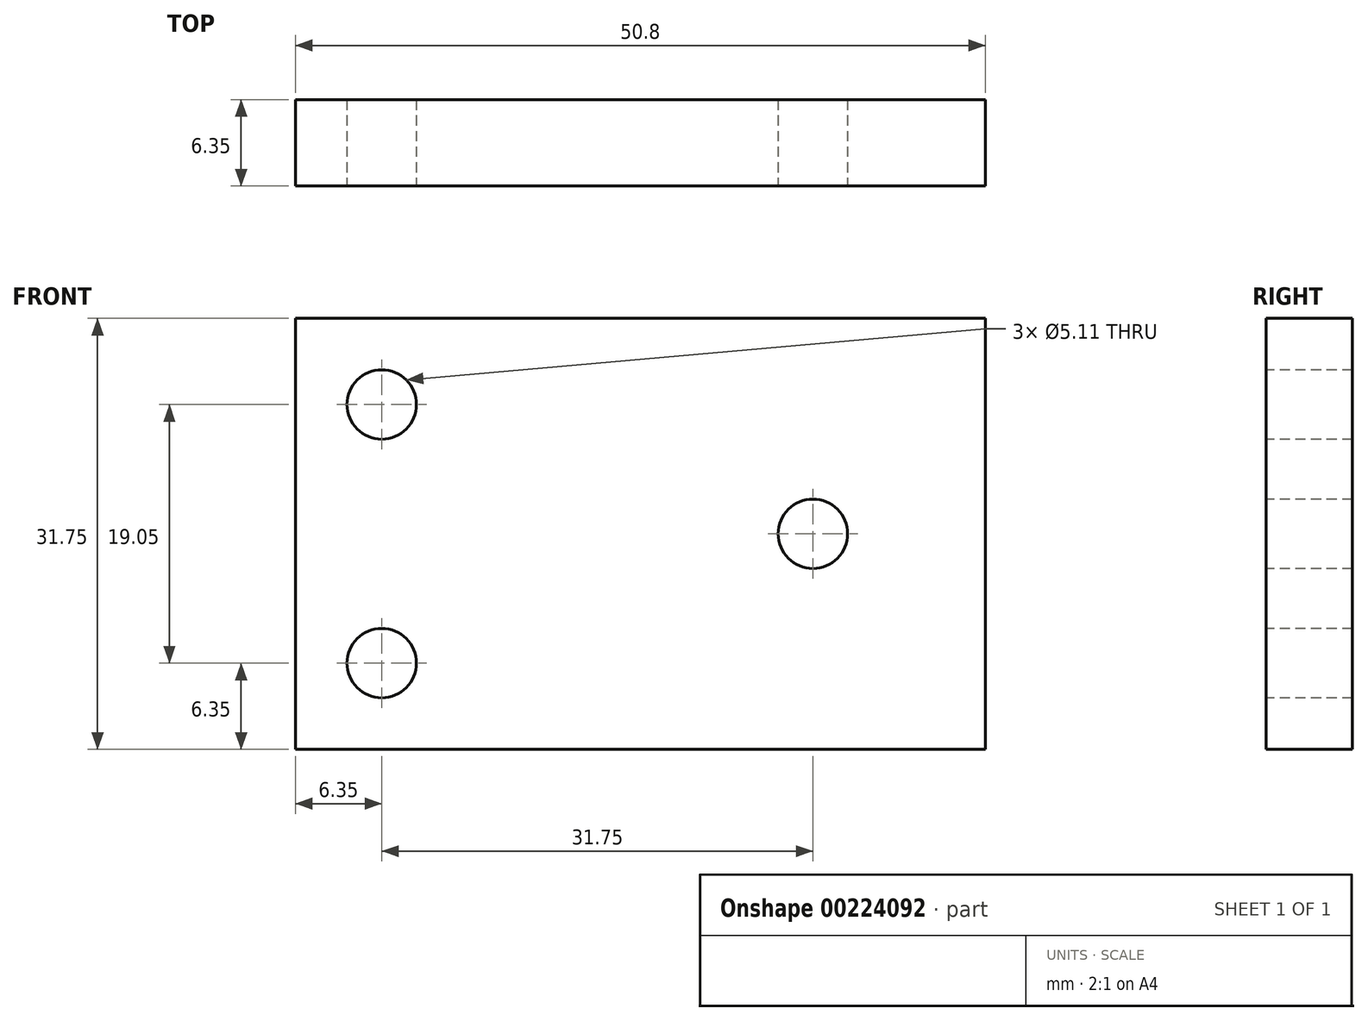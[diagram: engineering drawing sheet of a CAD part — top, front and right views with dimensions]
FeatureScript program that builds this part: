
annotation { "Feature Type Name" : "Feature", "Feature Type Description" : "" }
export const myFeature = defineFeature(function(context is Context, id is Id, definition is map)
    precondition{}
    {
        {
            var Q0;
            Q0=qCreatedBy(makeId("Front.planeOp"),FACE);
            var sketch = newSketch(context, id + "F0", { "sketchPlane" : qUnion([Q0])});
            skLineSegment(sketch, "E0.bottom", {"start": v(0, 0) * mm, "end": v(50.8, 0) * mm});
            skLineSegment(sketch, "E0.top", {"start": v(0, 31.75) * mm, "end": v(50.8, 31.75) * mm});
            skLineSegment(sketch, "E0.left", {"start": v(0, 0) * mm, "end": v(0, 31.75) * mm});
            skLineSegment(sketch, "E0.right", {"start": v(50.8, 0) * mm, "end": v(50.8, 31.75) * mm});
            skSolve(sketch);
        }
        {
            var Q0;
            Q0 = qSketchRegion(id + "F0", true);
            extrude(context, id + "F1", {"entities" : qUnion([Q0]), "depth" : 6.35 * mm});
        }
        {
            var Q0;
            Q0=makeQuery(id+"F1.opExtrude","CAP_FACE",FACE,{"disambiguationData":[OSD([sQuery(id+"F0.wireOp",EDGE,"E0.bottom"),sQuery(id+"F0.wireOp",EDGE,"E0.top"),sQuery(id+"F0.wireOp",EDGE,"E0.left"),sQuery(id+"F0.wireOp",EDGE,"E0.right")])],"isStart":false});
            var sketch = newSketch(context, id + "F2", { "sketchPlane" : qUnion([Q0])});
            skPoint(sketch, "E1", {"position": v(6.35, 25.4) * mm});
            skPoint(sketch, "E2", {"position": v(6.35, 6.35) * mm});
            skPoint(sketch, "E3", {"position": v(38.1, 15.88) * mm});
            skSolve(sketch);
        }
        {
            var Q0;
            Q0=sQuery(id+"F2.wireOp",VERTEX,"E1");
            var Q1;
            Q1=sQuery(id+"F2.wireOp",VERTEX,"E2");
            var Q2;
            Q2=sQuery(id+"F2.wireOp",VERTEX,"E3");
            var Q3;
            Q3=makeQuery(id+"F1.opExtrude","SWEPT_BODY",BODY,{"disambiguationData":[OSD([sQuery(id+"F0.wireOp",EDGE,"E0.bottom"),sQuery(id+"F0.wireOp",EDGE,"E0.top"),sQuery(id+"F0.wireOp",EDGE,"E0.left"),sQuery(id+"F0.wireOp",EDGE,"E0.right")])]});
            hole(context, id + "F3", {"style" : HoleStyle.SIMPLE, "endStyle" : HoleEndStyle.THROUGH, "standardTappedOrClearance" : lookupTablePath({ "standard" : "ANSI", "fit" : "Normal (ASME)", "size" : "#10", "type" : "Clearance" }), "standardBlindInLast" : lookupTablePath({ "fit" : "Free", "standard" : "ANSI", "size" : "#10", "type" : "Clearance" }), "holeDiameter" : 5.1 * mm, "locations" : qUnion([Q0, Q1, Q2]), "scope" : qUnion([Q3]), "isTappedThrough" : true});
        }
    });
